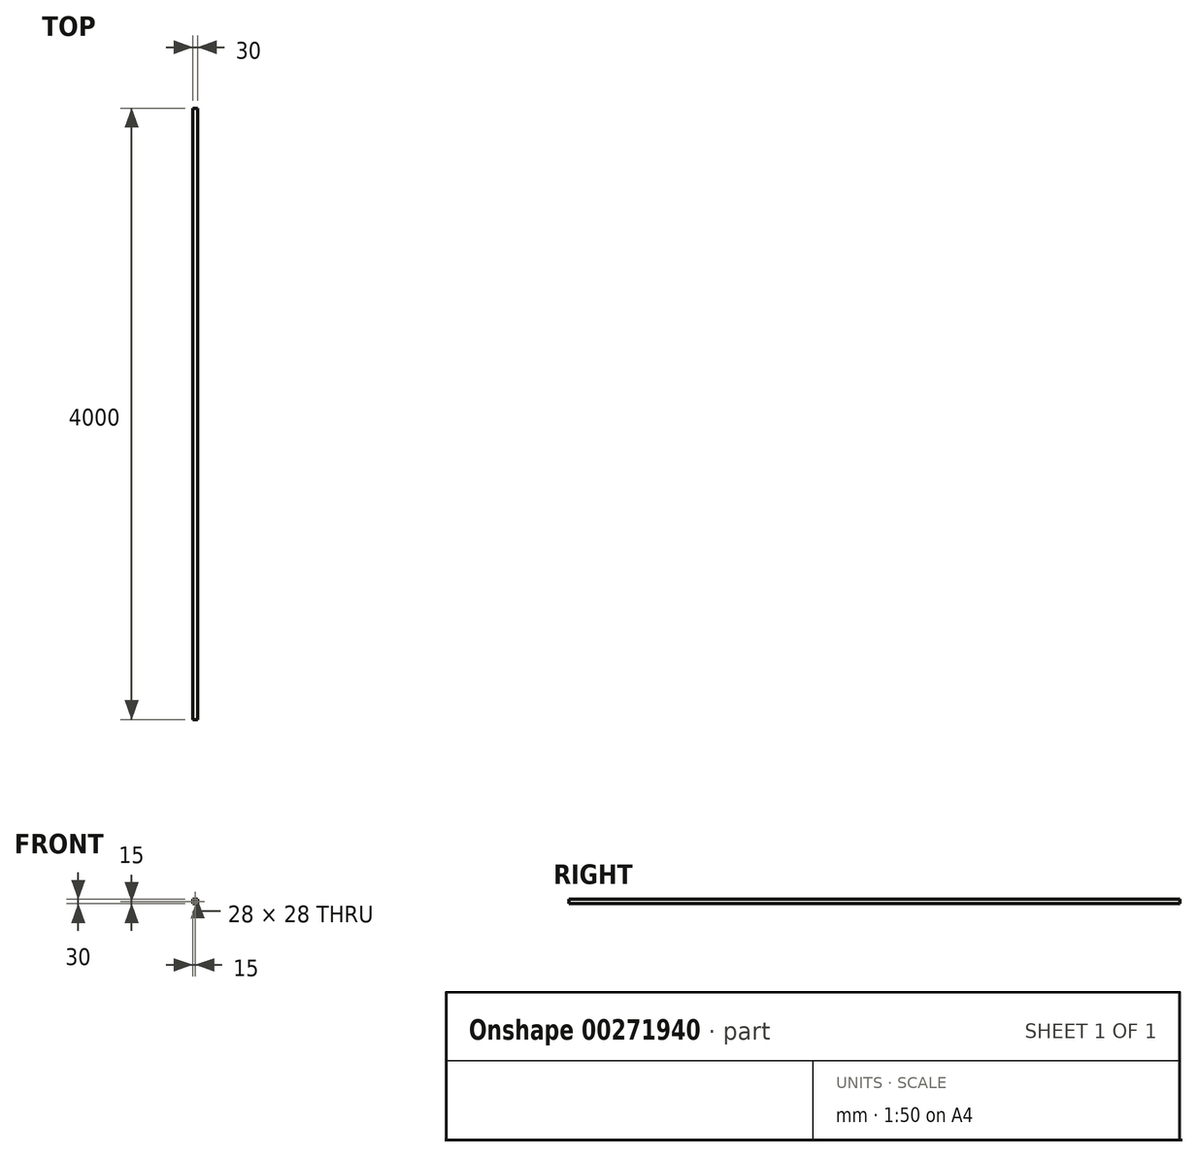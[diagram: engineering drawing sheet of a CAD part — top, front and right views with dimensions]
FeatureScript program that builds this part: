
annotation { "Feature Type Name" : "Feature", "Feature Type Description" : "" }
export const myFeature = defineFeature(function(context is Context, id is Id, definition is map)
    precondition{}
    {
        {
            var Q0;
            Q0=qCreatedBy(makeId("Front.planeOp"),FACE);
            var sketch = newSketch(context, id + "F0", { "sketchPlane" : qUnion([Q0])});
            skLineSegment(sketch, "E0.bottom", {"start": v(15, 15) * mm, "end": v(-15, 15) * mm});
            skLineSegment(sketch, "E0.top", {"start": v(15, -15) * mm, "end": v(-15, -15) * mm});
            skLineSegment(sketch, "E0.left", {"start": v(15, 15) * mm, "end": v(15, -15) * mm});
            skLineSegment(sketch, "E0.right", {"start": v(-15, 15) * mm, "end": v(-15, -15) * mm});
            skPoint(sketch, "E0.middle", {"position": v(0, 0) * mm});
            skLineSegment(sketch, "E1.bottom", {"start": v(14, 14) * mm, "end": v(-14, 14) * mm});
            skLineSegment(sketch, "E1.top", {"start": v(14, -14) * mm, "end": v(-14, -14) * mm});
            skLineSegment(sketch, "E1.left", {"start": v(14, 14) * mm, "end": v(14, -14) * mm});
            skLineSegment(sketch, "E1.right", {"start": v(-14, 14) * mm, "end": v(-14, -14) * mm});
            skSolve(sketch);
        }
        {
            var Q0;
            Q0=makeQuery(id+"F0.imprint","IMPRINT",FACE,{"disambiguationData":[TD([[makeQuery(id+"F0.imprint","IMPRINT",EDGE,{"derivedFrom":sQuery(id+"F0.wireOp",EDGE,"E0.bottom")}),1.0]])]});
            extrude(context, id + "F1", {"entities" : qUnion([Q0]), "depth" : 4000 * mm});
        }
    });
